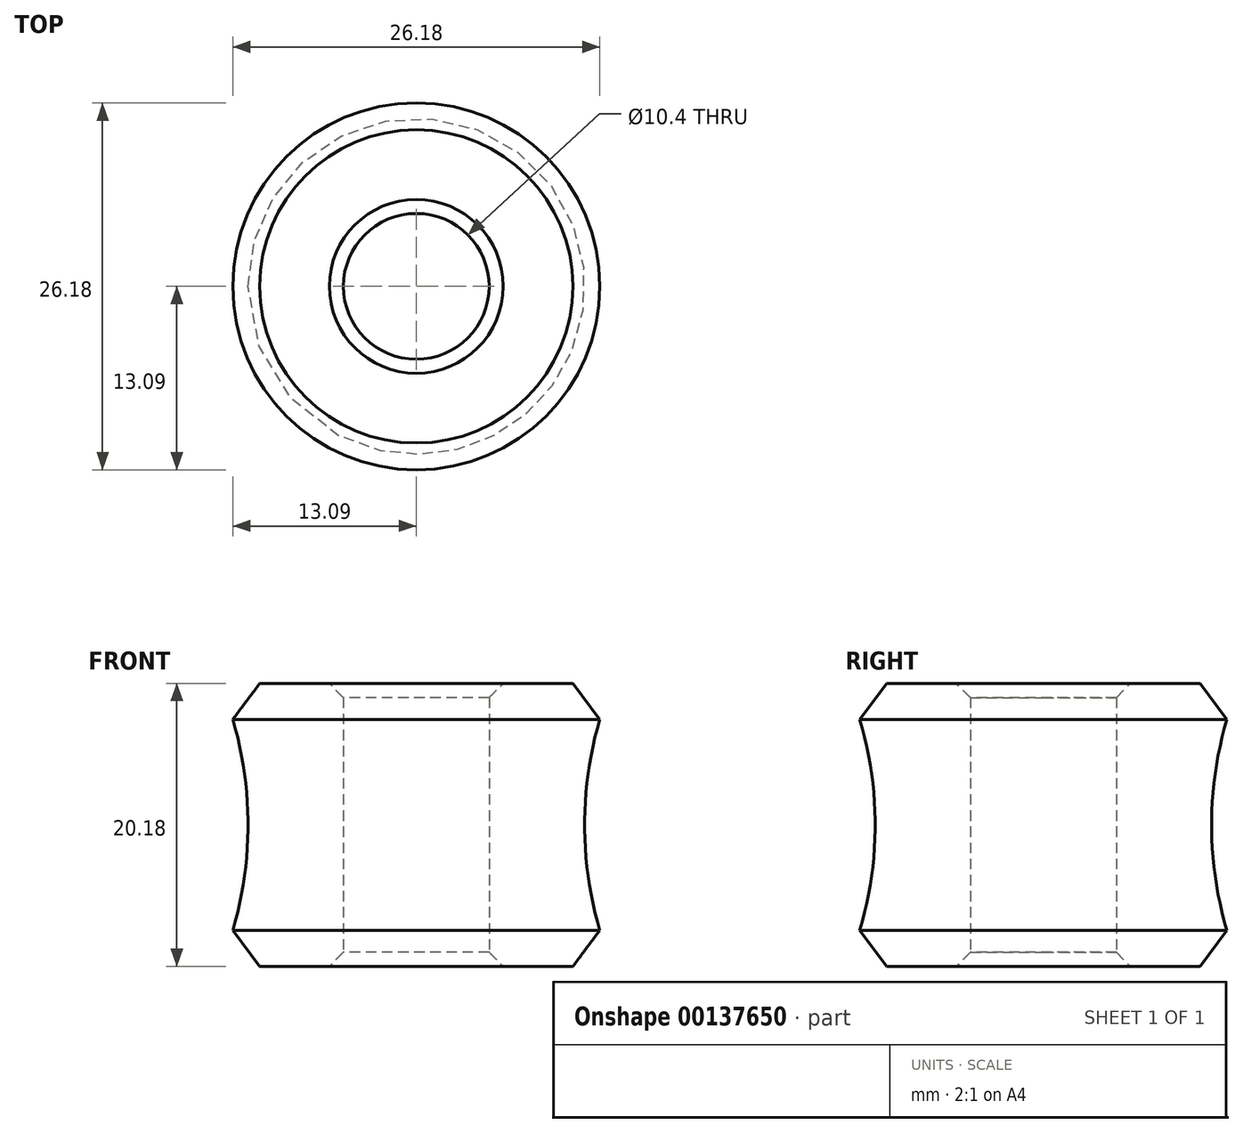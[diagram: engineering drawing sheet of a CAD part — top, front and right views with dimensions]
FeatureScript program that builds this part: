
annotation { "Feature Type Name" : "Feature", "Feature Type Description" : "" }
export const myFeature = defineFeature(function(context is Context, id is Id, definition is map)
    precondition{}
    {
        {
            var Q0;
            Q0=qCreatedBy(makeId("Front.planeOp"),FACE);
            var sketch = newSketch(context, id + "F0", { "sketchPlane" : qUnion([Q0])});
            skLineSegment(sketch, "E0", {"start": v(0, 0) * mm, "end": v(0, 20.18) * mm, "construction": true});
            skLineSegment(sketch, "E1", {"start": v(-12, 20.18) * mm, "end": v(-12, 0) * mm, "construction": true});
            skLineSegment(sketch, "E2", {"start": v(-14, 20.18) * mm, "end": v(-14, 0) * mm, "construction": true});
            skPoint(sketch, "E3", {"position": v(-12, 10.09) * mm});
            skLineSegment(sketch, "E4", {"start": v(-5.2, 20.18) * mm, "end": v(-5.2, 0) * mm});
            skLineSegment(sketch, "E5", {"start": v(-14, 20.18) * mm, "end": v(-5.2, 20.18) * mm});
            skLineSegment(sketch, "E6", {"start": v(-14, 0) * mm, "end": v(-5.2, 0) * mm});
            skArc(sketch, "E7", {"start": v(-14, 0) * mm, "mid": v(-12, 10.09) * mm, "end": v(-14, 20.18) * mm});
            skSolve(sketch);
        }
        {
            var Q0;
            Q0=makeQuery(id+"F0.imprint","IMPRINT",FACE,{"disambiguationData":[TD([[makeQuery(id+"F0.imprint","IMPRINT",EDGE,{"derivedFrom":sQuery(id+"F0.wireOp",EDGE,"E4")}),-1.0]])]});
            var Q1;
            Q1=sQuery(id+"F0.wireOp",EDGE,"E0");
            revolve(context, id + "F1", {"entities" : qUnion([Q0]), "axis" : qUnion([Q1]), "revolveType" : RevolveType.FULL});
        }
        {
            var Q0;
            Q0=makeQuery(id+"F1.opRevolve","SWEPT_FACE",FACE,{"disambiguationData":[OSD([sQuery(id+"F0.wireOp",EDGE,"E4")])]});
            chamfer(context, id + "F2", {"entities" : qUnion([Q0]), "width" : 1 * mm, "tangentPropagation" : true});
        }
        {
            var Q0;
            Q0=makeQuery(id+"F1.opRevolve","SWEPT_FACE",FACE,{"disambiguationData":[OSD([sQuery(id+"F0.wireOp",EDGE,"E7")])]});
            chamfer(context, id + "F3", {"entities" : qUnion([Q0]), "width" : 2 * mm, "tangentPropagation" : true});
        }
    });
